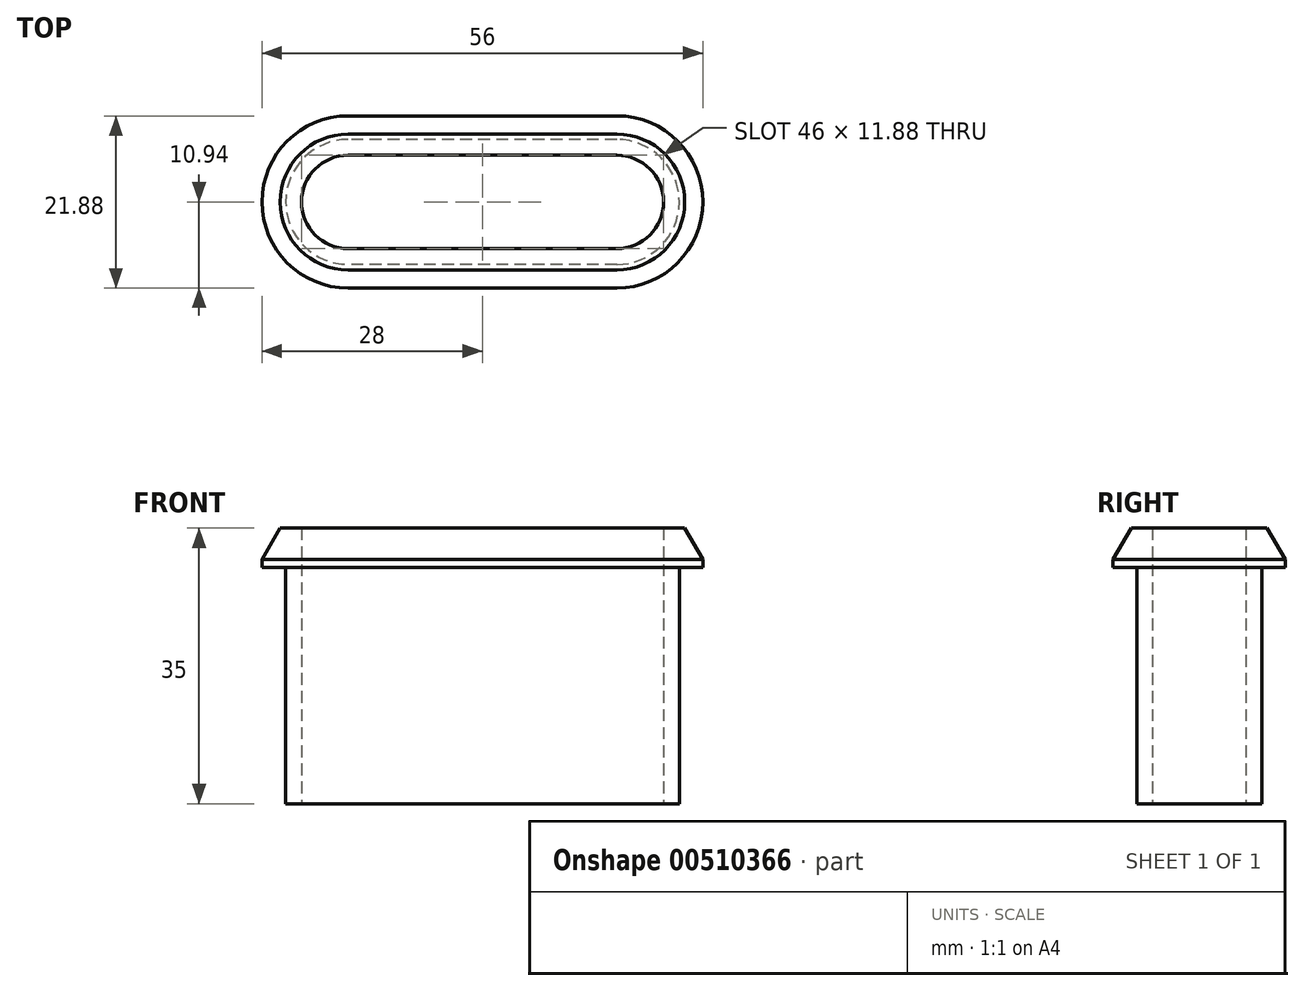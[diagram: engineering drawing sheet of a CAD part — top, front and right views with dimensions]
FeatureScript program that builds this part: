
annotation { "Feature Type Name" : "Feature", "Feature Type Description" : "" }
export const myFeature = defineFeature(function(context is Context, id is Id, definition is map)
    precondition{}
    {
        {
            var Q0;
            Q0=qCreatedBy(makeId("Top.planeOp"),FACE);
            var sketch = newSketch(context, id + "F0", { "sketchPlane" : qUnion([Q0])});
            skLineSegment(sketch, "E0.bottom", {"start": v(0, -7.94) * mm, "end": v(-17.06, -7.94) * mm});
            skLineSegment(sketch, "E0.top", {"start": v(0, 7.94) * mm, "end": v(-17.06, 7.94) * mm});
            skPoint(sketch, "E0.middle", {"position": v(0, 0) * mm});
            skArc(sketch, "E1", {"start": v(-17.06, 7.94) * mm, "mid": v(-25, 0) * mm, "end": v(-17.06, -7.94) * mm});
            skPoint(sketch, "E2.center.orphan", {"position": v(-25, 0) * mm});
            skPoint(sketch, "E3.MirrorP", {"position": v(25, 0) * mm});
            skLineSegment(sketch, "E4.MirrorCS", {"start": v(0, 7.94) * mm, "end": v(17.06, 7.94) * mm});
            skLineSegment(sketch, "E5.MirrorCS", {"start": v(0, -7.94) * mm, "end": v(17.06, -7.94) * mm});
            skArc(sketch, "E6.MirrorC", {"start": v(17.06, 7.94) * mm, "mid": v(25, 0) * mm, "end": v(17.06, -7.94) * mm});
            skLineSegment(sketch, "E7.0", {"start": v(0, 5.94) * mm, "end": v(17.06, 5.94) * mm});
            skLineSegment(sketch, "E7.1", {"start": v(0, -5.94) * mm, "end": v(17.06, -5.94) * mm});
            skLineSegment(sketch, "E7.2", {"start": v(0, -5.94) * mm, "end": v(-17.06, -5.94) * mm});
            skArc(sketch, "E7.3", {"start": v(17.06, 5.94) * mm, "mid": v(23, 0) * mm, "end": v(17.06, -5.94) * mm});
            skArc(sketch, "E7.4", {"start": v(-17.06, 5.94) * mm, "mid": v(-23, 0) * mm, "end": v(-17.06, -5.94) * mm});
            skLineSegment(sketch, "E7.5", {"start": v(0, 5.94) * mm, "end": v(-17.06, 5.94) * mm});
            skSolve(sketch);
        }
        {
            var Q0;
            Q0=makeQuery(id+"F0.imprint","IMPRINT",FACE,{"disambiguationData":[TD([[makeQuery(id+"F0.imprint","IMPRINT",EDGE,{"derivedFrom":sQuery(id+"F0.wireOp",EDGE,"E0.bottom")}),-1.0]])]});
            extrude(context, id + "F1", {"entities" : qUnion([Q0]), "depth" : 30 * mm});
        }
        {
            var Q0;
            Q0=makeQuery(id+"F1.opExtrude","CAP_FACE",FACE,{"disambiguationData":[OSD([sQuery(id+"F0.wireOp",EDGE,"E0.bottom"),sQuery(id+"F0.wireOp",EDGE,"E0.top"),sQuery(id+"F0.wireOp",EDGE,"E1"),sQuery(id+"F0.wireOp",EDGE,"E4.MirrorCS"),sQuery(id+"F0.wireOp",EDGE,"E5.MirrorCS"),sQuery(id+"F0.wireOp",EDGE,"E6.MirrorC"),sQuery(id+"F0.wireOp",EDGE,"E7.0"),sQuery(id+"F0.wireOp",EDGE,"E7.1"),sQuery(id+"F0.wireOp",EDGE,"E7.2"),sQuery(id+"F0.wireOp",EDGE,"E7.3"),sQuery(id+"F0.wireOp",EDGE,"E7.4"),sQuery(id+"F0.wireOp",EDGE,"E7.5")])],"isStart":false});
            var sketch = newSketch(context, id + "F2", { "sketchPlane" : qUnion([Q0])});
            skLineSegment(sketch, "E8.0", {"start": v(17.06, 5.94) * mm, "end": v(-17.06, 5.94) * mm});
            skArc(sketch, "E8.1", {"start": v(-17.06, 5.94) * mm, "mid": v(-23, 0) * mm, "end": v(-17.06, -5.94) * mm});
            skLineSegment(sketch, "E8.2", {"start": v(-17.06, -5.94) * mm, "end": v(17.06, -5.94) * mm});
            skArc(sketch, "E8.3", {"start": v(17.06, 5.94) * mm, "mid": v(23, 0) * mm, "end": v(17.06, -5.94) * mm});
            skLineSegment(sketch, "E9.0", {"start": v(17.06, 10.94) * mm, "end": v(-17.06, 10.94) * mm});
            skArc(sketch, "E9.1", {"start": v(17.06, 10.94) * mm, "mid": v(28, 0) * mm, "end": v(17.06, -10.94) * mm});
            skLineSegment(sketch, "E9.2", {"start": v(-17.06, -10.94) * mm, "end": v(17.06, -10.94) * mm});
            skArc(sketch, "E9.3", {"start": v(-17.06, 10.94) * mm, "mid": v(-28, 0) * mm, "end": v(-17.06, -10.94) * mm});
            skSolve(sketch);
        }
        {
            var Q0;
            Q0=makeQuery(id+"F2.imprint","IMPRINT",FACE,{"disambiguationData":[TD([[makeQuery(id+"F2.imprint","IMPRINT",EDGE,{"derivedFrom":sQuery(id+"F2.wireOp",EDGE,"E8.0")}),-1.0]])]});
            var Q1;
            Q1=makeQuery(id+"F2.imprint","IMPRINT",FACE,{"disambiguationData":[TD([[makeQuery(id+"F2.imprint","IMPRINT",EDGE,{"derivedFrom":sQuery(id+"F2.wireOp",EDGE,"E9.0")}),1.0]])]});
            extrude(context, id + "F3", {"entities" : qUnion([Q0, Q1]), "operationType" : NewBodyOperationType.ADD, "depth" : 5 * mm});
        }
        {
            var Q0;
            Q0=makeQuery(id+"F3.opExtrude","CAP_EDGE",EDGE,{"disambiguationData":[OSD([sQuery(id+"F2.wireOp",EDGE,"E9.3")])],"isStart":false});
            var Q1;
            Q1=makeQuery(id+"F3.opExtrude","CAP_EDGE",EDGE,{"disambiguationData":[OSD([sQuery(id+"F2.wireOp",EDGE,"E9.2")])],"isStart":false});
            var Q2;
            Q2=makeQuery(id+"F3.opExtrude","CAP_EDGE",EDGE,{"disambiguationData":[OSD([sQuery(id+"F2.wireOp",EDGE,"E9.1")])],"isStart":false});
            var Q3;
            Q3=makeQuery(id+"F3.opExtrude","CAP_EDGE",EDGE,{"disambiguationData":[OSD([sQuery(id+"F2.wireOp",EDGE,"E9.0")])],"isStart":false});
            chamfer(context, id + "F4", {"entities" : qUnion([Q0, Q1, Q2, Q3]), "chamferType" : ChamferType.OFFSET_ANGLE, "width" : 4 * mm, "oppositeDirection" : true, "angle" : 30 * degree, "tangentPropagation" : true});
        }
    });
